# Revit family: НЕВАТОМ_Диффузор ДП4_20220407
name_source: partatom
category: Воздухораспределители
revit_build: Autodesk Revit 2017 (Build: 20170118_1100(x64)
units: mm (PartAtom-declared; Revit-internal decimal feet)

## family parameters
Всегда вертикально = Да
На основе рабочей плоскости = Нет
Общий = Нет
При загрузке вырезать с полостями = Нет
Размер круглого соединителя = Использовать диаметр
Тип детали = Нормальный
Точка расчета площади = Нет

## types (3) — shared parameters
ADSK_Единица измерения = шт.
ADSK_Завод-изготовитель = NEVATOM
ADSK_Материал наименование = Алюминий
ADSK_Наименование = Диффузор потолочный
ADSK_Размер_Ширина = 50 мм
Nevatom_URL = https://t.me
h = 50 мм
Ключевая пометка = Вентиляция
Материал = RAL 9016
zero-valued in all types: ADSK_Масса

## per-type parameters (varying)
| type | 1 | A | ADSK_Размер_Высота | ADSK_Размер_Длина | a | ΔPmax | ΔPmin | Макс. расход | Макс. расход воздуха | Мин. расход | Минимальный расход воздуха |
| ДП4 600х600 | 100 мм | 595 мм | 595 мм | 595 мм | 447 мм | 41.0 Па | 0.4 Па | 3500.0 м³/ч | 3500.0 м³/ч | 350.0 м³/ч | 350.0 м³/ч |
| ДП4 450х450 | 169 мм | 445 мм | 445 мм | 445 мм | 297 мм | 41.0 Па | 0.4 Па | 1500.0 м³/ч | 1500.0 м³/ч | 150.0 м³/ч | 150.0 м³/ч |
| ДП4 300х300 | 169 мм | 295 мм | 295 мм | 295 мм | 147 мм | 98.0 Па | 0.9 Па | 500.0 м³/ч | 500.0 м³/ч | 50.0 м³/ч | 50.0 м³/ч |

note: column(s) folded — value = type name in every type: ADSK_Марка
